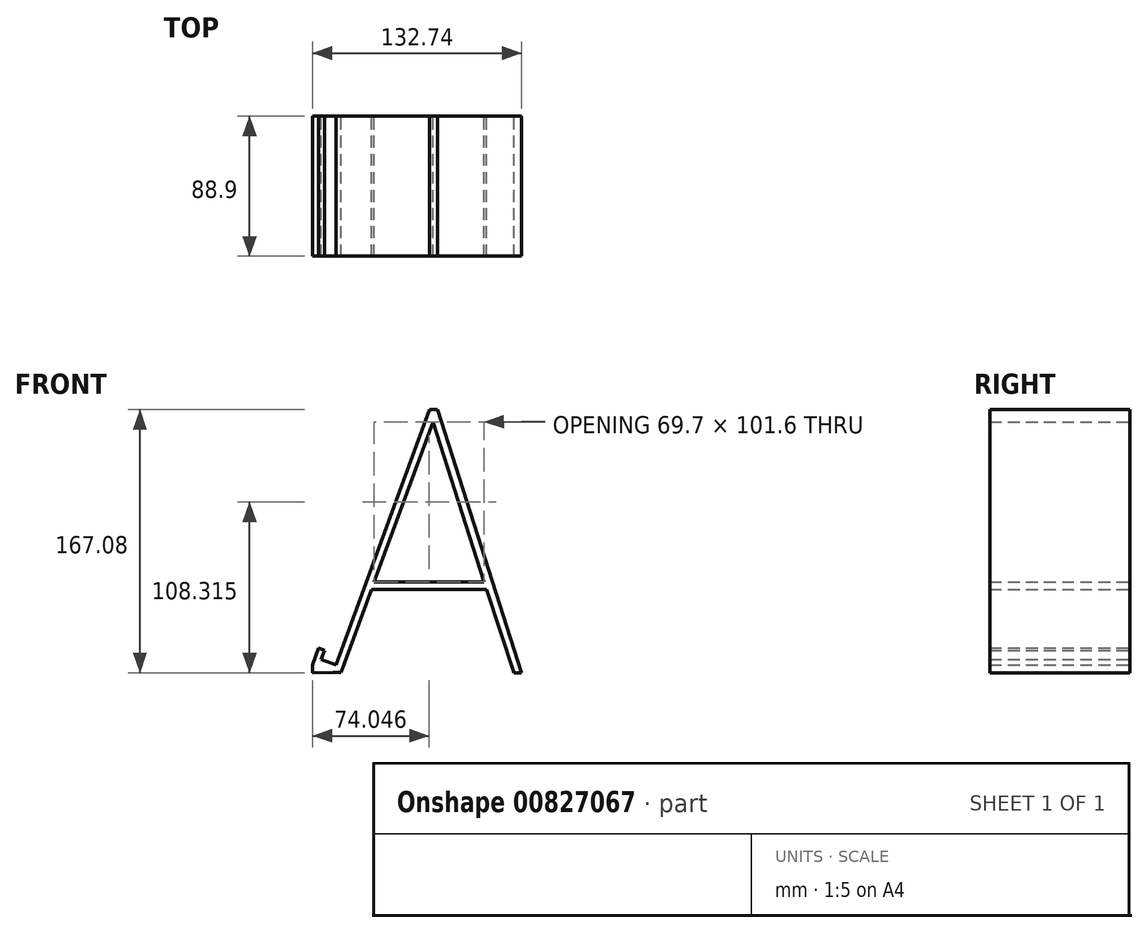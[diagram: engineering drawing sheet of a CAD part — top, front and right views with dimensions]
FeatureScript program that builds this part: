
annotation { "Feature Type Name" : "Feature", "Feature Type Description" : "" }
export const myFeature = defineFeature(function(context is Context, id is Id, definition is map)
    precondition{}
    {
        {
            var Q0;
            Q0=qCreatedBy(makeId("Front.planeOp"),FACE);
            var sketch = newSketch(context, id + "F0", { "sketchPlane" : qUnion([Q0])});
            skLineSegment(sketch, "E0", {"start": v(0, 167.08) * mm, "end": v(-5.07, 167.08) * mm});
            skLineSegment(sketch, "E1", {"start": v(-61.15, 0.13) * mm, "end": v(-66.22, 0.13) * mm});
            skLineSegment(sketch, "E2", {"start": v(-79.33, 4.9) * mm, "end": v(-77.6, 9.67) * mm});
            skLineSegment(sketch, "E3", {"start": v(-73.94, 8.34) * mm, "end": v(-64.48, 4.9) * mm});
            skLineSegment(sketch, "E4", {"start": v(-64.48, 4.9) * mm, "end": v(-5.07, 167.08) * mm});
            skLineSegment(sketch, "E5", {"start": v(-77.6, 9.67) * mm, "end": v(-75.42, 15.64) * mm});
            skLineSegment(sketch, "E6", {"start": v(-75.42, 15.64) * mm, "end": v(-71.77, 14.3) * mm});
            skLineSegment(sketch, "E7", {"start": v(-71.77, 14.3) * mm, "end": v(-73.94, 8.34) * mm});
            skLineSegment(sketch, "E8", {"start": v(0, 167.08) * mm, "end": v(53.41, 0) * mm});
            skLineSegment(sketch, "E9", {"start": v(53.41, 0) * mm, "end": v(48.65, 0) * mm});
            skLineSegment(sketch, "E10", {"start": v(-2.92, 57.51) * mm, "end": v(-40.13, 57.51) * mm});
            skLineSegment(sketch, "E11.0", {"start": v(-2.92, 52.75) * mm, "end": v(-41.88, 52.75) * mm});
            skLineSegment(sketch, "E12", {"start": v(-2.92, 57.51) * mm, "end": v(29.56, 57.51) * mm});
            skLineSegment(sketch, "E13", {"start": v(-2.92, 52.75) * mm, "end": v(31.09, 52.75) * mm});
            skLineSegment(sketch, "E14", {"start": v(-2.92, 159.11) * mm, "end": v(29.56, 57.51) * mm});
            skLineSegment(sketch, "E15", {"start": v(31.09, 52.75) * mm, "end": v(48.65, 0) * mm});
            skLineSegment(sketch, "E16", {"start": v(-2.92, 159.11) * mm, "end": v(-40.13, 57.51) * mm});
            skLineSegment(sketch, "E17", {"start": v(-41.88, 52.75) * mm, "end": v(-61.15, 0.13) * mm});
            skLineSegment(sketch, "E18", {"start": v(-66.22, 0.13) * mm, "end": v(-79.33, 0) * mm});
            skLineSegment(sketch, "E19", {"start": v(-79.33, 0) * mm, "end": v(-79.33, 4.9) * mm});
            skSolve(sketch);
        }
        {
            var Q0;
            Q0 = qSketchRegion(id + "F0", true);
            extrude(context, id + "F1", {"entities" : qUnion([Q0]), "depth" : 88.9 * mm, "offsetDistance" : 25.4 * mm});
        }
    });
